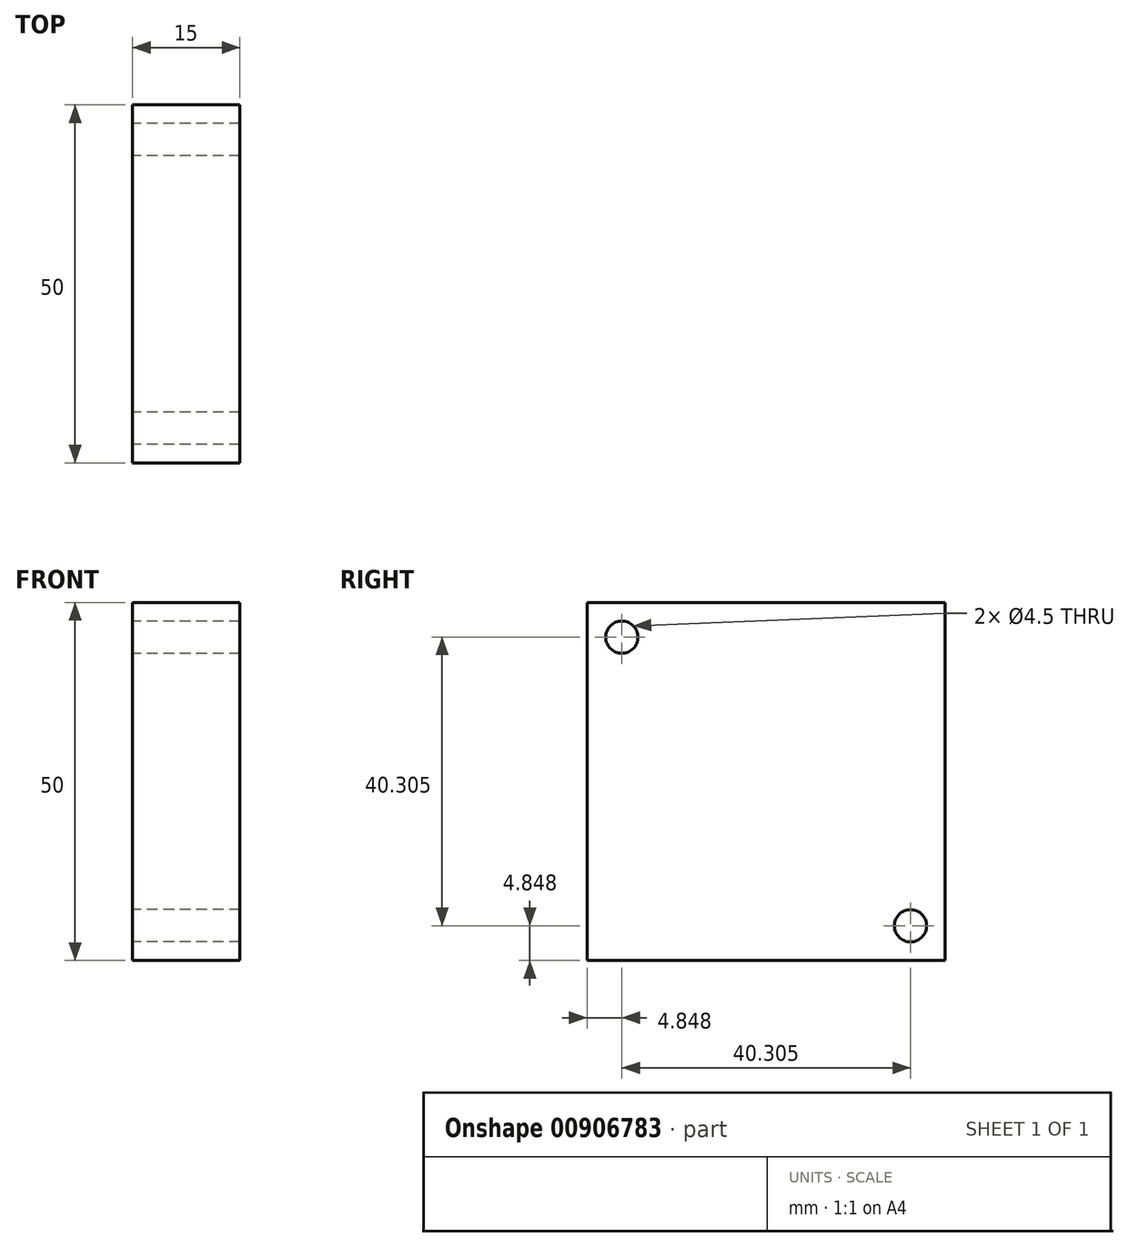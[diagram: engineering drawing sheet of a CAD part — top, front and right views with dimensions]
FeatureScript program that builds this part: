
annotation { "Feature Type Name" : "Feature", "Feature Type Description" : "" }
export const myFeature = defineFeature(function(context is Context, id is Id, definition is map)
    precondition{}
    {
        {
            var Q0;
            Q0=qCreatedBy(makeId("Right.planeOp"),FACE);
            var sketch = newSketch(context, id + "F0", { "sketchPlane" : qUnion([Q0])});
            skLineSegment(sketch, "E0.bottom", {"start": v(-25, 25) * mm, "end": v(25, 25) * mm});
            skLineSegment(sketch, "E0.top", {"start": v(-25, -25) * mm, "end": v(25, -25) * mm});
            skLineSegment(sketch, "E0.left", {"start": v(-25, 25) * mm, "end": v(-25, -25) * mm});
            skLineSegment(sketch, "E0.right", {"start": v(25, 25) * mm, "end": v(25, -25) * mm});
            skPoint(sketch, "E0.middle", {"position": v(0, 0) * mm});
            skCircle(sketch, "E1", {"center": v(-20.15, 20.15) * mm, "radius": 2.25 * mm});
            skLineSegment(sketch, "E2", {"start": v(25, 25) * mm, "end": v(-25, -25) * mm, "construction": true});
            skCircle(sketch, "E3.MirrorC", {"center": v(20.15, -20.15) * mm, "radius": 2.25 * mm});
            skLineSegment(sketch, "E4", {"start": v(-20.15, 20.15) * mm, "end": v(-20.15, 25) * mm, "construction": true});
            skLineSegment(sketch, "E5", {"start": v(-20.15, 20.15) * mm, "end": v(-25, 20.15) * mm, "construction": true});
            skSolve(sketch);
        }
        {
            var Q0;
            Q0=makeQuery(id+"F0.imprint","IMPRINT",FACE,{"disambiguationData":[TD([[makeQuery(id+"F0.imprint","IMPRINT",EDGE,{"derivedFrom":sQuery(id+"F0.wireOp",EDGE,"E0.bottom")}),-1.0]])]});
            extrude(context, id + "F1", {"entities" : qUnion([Q0]), "depth" : 15 * mm, "offsetDistance" : 25 * mm});
        }
    });
